annotation { "Feature Type Name" : "Feature", "Feature Type Description" : "" }
export const myFeature = defineFeature(function(context is Context, id is Id, definition is map)
    precondition{}
    {
        {
            var Q0;
            Q0=qCreatedBy(makeId("Right.planeOp"),FACE);
            var sketch = newSketch(context, id + "F0", { "sketchPlane" : qUnion([Q0])});
            skLineSegment(sketch, "E0", {"start": v(0, 0) * mm, "end": v(-4572, 0) * mm});
            skLineSegment(sketch, "E1", {"start": v(0, 0) * mm, "end": v(4572, 0) * mm});
            skLineSegment(sketch, "E2", {"start": v(0, 0) * mm, "end": v(0, -2286) * mm});
            skLineSegment(sketch, "E3", {"start": v(0, -2286) * mm, "end": v(4572, 0) * mm});
            skLineSegment(sketch, "E4", {"start": v(0, -2286) * mm, "end": v(-4572, 0) * mm});
            skLineSegment(sketch, "E5", {"start": v(0, -2286) * mm, "end": v(0, -2743.2) * mm});
            skLineSegment(sketch, "E6", {"start": v(4572, 0) * mm, "end": v(5486.4, 0) * mm});
            skLineSegment(sketch, "E7", {"start": v(5486.4, 0) * mm, "end": v(0, -2743.2) * mm});
            skLineSegment(sketch, "E8", {"start": v(-4572, 0) * mm, "end": v(-5486.4, 0) * mm});
            skLineSegment(sketch, "E9", {"start": v(-5486.4, 0) * mm, "end": v(0, -2743.2) * mm});
            skLineSegment(sketch, "E10", {"start": v(4572, 0) * mm, "end": v(4572, 3352.8) * mm});
            skLineSegment(sketch, "E11", {"start": v(-4572, 0) * mm, "end": v(-4572, 3352.8) * mm});
            skLineSegment(sketch, "E12", {"start": v(4572, 3352.8) * mm, "end": v(-4572, 3352.8) * mm});
            skLineSegment(sketch, "E13", {"start": v(-4572, 3352.8) * mm, "end": v(-4572, 3962.4) * mm});
            skLineSegment(sketch, "E14", {"start": v(4572, 3352.8) * mm, "end": v(4572, 3962.4) * mm});
            skLineSegment(sketch, "E15", {"start": v(4572, 3962.4) * mm, "end": v(-4572, 3962.4) * mm});
            skLineSegment(sketch, "E16", {"start": v(-4572, 3962.4) * mm, "end": v(-9144, 3962.4) * mm});
            skLineSegment(sketch, "E17", {"start": v(-4572, 3352.8) * mm, "end": v(-9158.45, 3352.8) * mm});
            skLineSegment(sketch, "E18", {"start": v(-9144, 3962.4) * mm, "end": v(-9158.45, 3352.8) * mm});
            skLineSegment(sketch, "E19", {"start": v(-9158.45, 3352.8) * mm, "end": v(-9158.45, 609.6) * mm});
            skLineSegment(sketch, "E20", {"start": v(-4572, 0) * mm, "end": v(-9158.45, 609.6) * mm});
            skLineSegment(sketch, "E21", {"start": v(-9158.45, 609.6) * mm, "end": v(-9158.45, 1219.2) * mm});
            skLineSegment(sketch, "E22", {"start": v(-9158.45, 1219.2) * mm, "end": v(-4572, 609.6) * mm});
            skLineSegment(sketch, "E23", {"start": v(3352.8, 1219.2) * mm, "end": v(3352.8, 3352.8) * mm});
            skLineSegment(sketch, "E24", {"start": v(3352.8, 1219.2) * mm, "end": v(2438.4, 1219.2) * mm});
            skLineSegment(sketch, "E25", {"start": v(2438.4, 1219.2) * mm, "end": v(2438.4, 3352.8) * mm});
            skLineSegment(sketch, "E26", {"start": v(2438.4, 3352.8) * mm, "end": v(2133.6, 3352.8) * mm});
            skLineSegment(sketch, "E27", {"start": v(2133.6, 3352.8) * mm, "end": v(2133.6, 882.78) * mm});
            skLineSegment(sketch, "E28", {"start": v(2133.6, 882.78) * mm, "end": v(3622.78, 882.78) * mm});
            skLineSegment(sketch, "E29", {"start": v(3352.8, 3352.8) * mm, "end": v(3657.6, 3352.8) * mm});
            skLineSegment(sketch, "E30", {"start": v(3657.6, 3352.8) * mm, "end": v(3622.78, 882.78) * mm});
            skPoint(sketch, "E31.endSnap0", {"position": v(-4572, 1676.4) * mm});
            skLineSegment(sketch, "E32", {"start": v(-3352.8, 540.77) * mm, "end": v(-3352.8, 1912.37) * mm});
            skLineSegment(sketch, "E33", {"start": v(-3352.8, 1912.37) * mm, "end": v(-609.6, 1912.37) * mm});
            skLineSegment(sketch, "E34", {"start": v(-3352.8, 540.77) * mm, "end": v(-609.6, 540.77) * mm});
            skLineSegment(sketch, "E35", {"start": v(-609.6, 1912.37) * mm, "end": v(-609.6, 540.77) * mm});
            skLineSegment(sketch, "E36", {"start": v(-609.6, 693.17) * mm, "end": v(-762, 693.17) * mm});
            skLineSegment(sketch, "E37", {"start": v(-762, 540.77) * mm, "end": v(-762, 693.17) * mm});
            skLineSegment(sketch, "E38", {"start": v(-762, 693.17) * mm, "end": v(-3097.86, 693.17) * mm});
            skLineSegment(sketch, "E39", {"start": v(-762, 693.17) * mm, "end": v(-762, 1687.9) * mm});
            skLineSegment(sketch, "E40", {"start": v(-762, 1687.9) * mm, "end": v(-3097.86, 1687.9) * mm});
            skLineSegment(sketch, "E41", {"start": v(-3097.86, 693.17) * mm, "end": v(-3097.86, 1687.9) * mm});
            skLineSegment(sketch, "E42", {"start": v(-6400.8, 1467.63) * mm, "end": v(-6400.8, 2686.83) * mm});
            skLineSegment(sketch, "E43", {"start": v(-6400.8, 1467.63) * mm, "end": v(-7620, 1467.63) * mm});
            skLineSegment(sketch, "E44", {"start": v(-7620, 1467.63) * mm, "end": v(-7620, 2686.83) * mm});
            skLineSegment(sketch, "E45", {"start": v(-6400.8, 2683.08) * mm, "end": v(-7620, 2686.83) * mm});
            skLineSegment(sketch, "E46", {"start": v(-6506.95, 1625.07) * mm, "end": v(-7496.04, 1625.07) * mm});
            skLineSegment(sketch, "E47", {"start": v(-6506.95, 1625.07) * mm, "end": v(-6506.95, 2495.47) * mm});
            skLineSegment(sketch, "E48", {"start": v(-7496.04, 1625.07) * mm, "end": v(-7496.04, 2482.28) * mm});
            skLineSegment(sketch, "E49", {"start": v(-6506.95, 2495.47) * mm, "end": v(-7496.04, 2482.28) * mm});
            skText(sketch, "E50", { "text": "Emma Crane", "fontName": "OpenSans-Regular.ttf"});
            const initialGuessF0  = {"E50": [-8.19469, -4.45341, 1, 0, 1.41525]};
            skSetInitialGuess(sketch, initialGuessF0);
            skSolve(sketch);
        }
        {
            var Q0;
            {var subQ13=sQuery(id+"F0.wireOp",EDGE,"E0");Q0=makeQuery(id+"F0.imprint","IMPRINT",FACE,{"disambiguationData":[TD([[makeQuery(id+"F0.imprint","IMPRINT",EDGE,{"derivedFrom":subQ13}),-1.0]])]});}
            var Q1;
            Q1=makeQuery(id+"F0.imprint","IMPRINT",FACE,{"disambiguationData":[TD([[makeQuery(id+"F0.imprint","IMPRINT",EDGE,{"derivedFrom":sQuery(id+"F0.wireOp",EDGE,"E1")}),-1.0]])]});
            var Q2;
            Q2=makeQuery(id+"F0.imprint","IMPRINT",FACE,{"disambiguationData":[TD([[makeQuery(id+"F0.imprint","IMPRINT",EDGE,{"derivedFrom":sQuery(id+"F0.wireOp",EDGE,"E0")}),1.0]])]});
            var Q3;
            Q3=makeQuery(id+"F0.imprint","IMPRINT",FACE,{"disambiguationData":[TD([[makeQuery(id+"F0.imprint","IMPRINT",EDGE,{"derivedFrom":sQuery(id+"F0.wireOp",EDGE,"E4")}),1.0]])]});
            var Q4;
            Q4=makeQuery(id+"F0.imprint","IMPRINT",FACE,{"disambiguationData":[TD([[makeQuery(id+"F0.imprint","IMPRINT",EDGE,{"derivedFrom":sQuery(id+"F0.wireOp",EDGE,"E3")}),-1.0]])]});
            var Q5;
            {var subQ1=sQuery(id+"F0.wireOp",EDGE,"E17");Q5=makeQuery(id+"F0.imprint","IMPRINT",FACE,{"disambiguationData":[TD([[makeQuery(id+"F0.imprint","IMPRINT",EDGE,{"derivedFrom":subQ1}),1.0]])]});}
            var Q6;
            {var subQ0=sQuery(id+"F0.wireOp",EDGE,"E20");Q6=makeQuery(id+"F0.imprint","IMPRINT",FACE,{"disambiguationData":[TD([[makeQuery(id+"F0.imprint","IMPRINT",EDGE,{"derivedFrom":subQ0}),-1.0]])]});}
            var Q7;
            Q7=makeQuery(id+"F0.imprint","IMPRINT",FACE,{"disambiguationData":[TD([[makeQuery(id+"F0.imprint","IMPRINT",EDGE,{"derivedFrom":sQuery(id+"F0.wireOp",EDGE,"E13")}),1.0]])]});
            var Q8;
            {var subQ0=sQuery(id+"F0.wireOp",EDGE,"E13");Q8=makeQuery(id+"F0.imprint","IMPRINT",FACE,{"disambiguationData":[TD([[makeQuery(id+"F0.imprint","IMPRINT",EDGE,{"derivedFrom":subQ0}),-1.0]])]});}
            extrude(context, id + "F1", {"entities" : qUnion([Q0, Q1, Q2, Q3, Q4, Q5, Q6, Q7, Q8]), "depth" : 8747.76 * mm, "offsetDistance" : 30.48 * mm});
        }
        {
            var Q0;
            Q0=makeQuery(id+"F0.imprint","IMPRINT",FACE,{"disambiguationData":[TD([[makeQuery(id+"F0.imprint","IMPRINT",EDGE,{"derivedFrom":sQuery(id+"F0.wireOp",EDGE,"E46")}),-1.0]])]});
            var Q1;
            Q1=makeQuery(id+"F0.imprint","IMPRINT",FACE,{"disambiguationData":[TD([[makeQuery(id+"F0.imprint","IMPRINT",EDGE,{"derivedFrom":sQuery(id+"F0.wireOp",EDGE,"E38")}),-1.0]])]});
            var Q2;
            {var subQ0=sQuery(id+"F0.wireOp",EDGE,"E23");Q2=makeQuery(id+"F0.imprint","IMPRINT",FACE,{"disambiguationData":[TD([[makeQuery(id+"F0.imprint","IMPRINT",EDGE,{"derivedFrom":subQ0}),1.0]])]});}
            extrude(context, id + "F2", {"entities" : qUnion([Q0, Q1, Q2]), "operationType" : NewBodyOperationType.ADD, "depth" : 8503.92 * mm, "offsetDistance" : 30.48 * mm});
        }
        {
            var Q0;
            Q0=makeQuery(id+"F0.imprint","IMPRINT",FACE,{"disambiguationData":[TD([[makeQuery(id+"F0.imprint","IMPRINT",EDGE,{"derivedFrom":sQuery(id+"F0.wireOp",EDGE,"E23")}),-1.0]])]});
            extrude(context, id + "F3", {"entities" : qUnion([Q0]), "operationType" : NewBodyOperationType.ADD, "depth" : 8656.32 * mm, "offsetDistance" : 30.48 * mm});
        }
        {
            var Q0;
            Q0=makeQuery(id+"F1.opExtrude","SWEPT_FACE",FACE,{"disambiguationData":[OSD([sQuery(id+"F0.wireOp",EDGE,"E10"),sQuery(id+"F0.wireOp",EDGE,"E14")])]});
            var sketch = newSketch(context, id + "F4", { "sketchPlane" : qUnion([Q0])});
            skLineSegment(sketch, "E51.bottom", {"start": v(-661.8, 960.74) * mm, "end": v(-3001.55, 960.74) * mm});
            skLineSegment(sketch, "E51.top", {"start": v(-661.8, 2376) * mm, "end": v(-3001.55, 2376) * mm});
            skLineSegment(sketch, "E51.left", {"start": v(-661.8, 960.74) * mm, "end": v(-661.8, 2376) * mm});
            skLineSegment(sketch, "E51.right", {"start": v(-3001.55, 960.74) * mm, "end": v(-3001.55, 2376) * mm});
            skLineSegment(sketch, "E52.bottom", {"start": v(-4298.28, 1080.34) * mm, "end": v(-6976.3, 1080.34) * mm});
            skLineSegment(sketch, "E52.top", {"start": v(-4298.28, 2336.12) * mm, "end": v(-6976.3, 2336.12) * mm});
            skLineSegment(sketch, "E52.left", {"start": v(-4298.28, 1080.34) * mm, "end": v(-4298.28, 2336.12) * mm});
            skLineSegment(sketch, "E52.right", {"start": v(-6976.3, 1080.34) * mm, "end": v(-6976.3, 2336.12) * mm});
            skSolve(sketch);
        }
        {
            var Q0;
            Q0=makeQuery(id+"F4.imprint","IMPRINT",FACE,{"disambiguationData":[TD([[makeQuery(id+"F4.imprint","IMPRINT",EDGE,{"derivedFrom":sQuery(id+"F4.wireOp",EDGE,"E51.bottom")}),-1.0]])]});
            var Q1;
            Q1=makeQuery(id+"F4.imprint","IMPRINT",FACE,{"disambiguationData":[TD([[makeQuery(id+"F4.imprint","IMPRINT",EDGE,{"derivedFrom":sQuery(id+"F4.wireOp",EDGE,"E52.bottom")}),-1.0]])]});
            extrude(context, id + "F5", {"entities" : qUnion([Q0, Q1]), "operationType" : NewBodyOperationType.ADD, "depth" : 213.36 * mm, "offsetDistance" : 30.48 * mm});
        }
    });